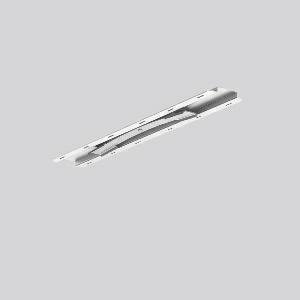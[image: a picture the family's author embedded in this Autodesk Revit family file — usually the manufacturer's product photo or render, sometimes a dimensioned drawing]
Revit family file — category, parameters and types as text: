
# Revit family: linedo_pendelset_verbinder_982680_000_81c2
name_source: partatom
category: Lighting Fixtures
units: mm (PartAtom-declared; Revit-internal decimal feet)

## family parameters
Cut with Voids When Loaded = No
Host = Face
Light Source = No
Part Type = Normal
Room Calculation Point = No
Round Connector Dimension = Use Diameter
Shared = No

## types (1)
- LINEDO Pendelset Verbinder
    Apparent Load = 0 VA
    Default Elevation = 1800 mm
    Description = Connector for suspended installation. Metal lever galvanised to mechanically connect 2 LINEDO suspended modules. A connector must be placed at each joint between modules.
Colour: zinc plated
Length: 300 mm
Width: 48 mm
Height: 9 mm
Weight: 182 g
    Height = 9 mm  [stored 0.0295276 ft]
    Lamp = 0 x
    Length = 300 mm
    Luminous efficacy = 0 lm/W
    Manufacturer = RZB
    ModVariant = No
    Model = 982680.000
    Mounting Place = Ceiling
    Mounting Type = Surface mounted
    Number of Poles = 1
    OnlyDefault = Yes
    Power Factor = 1
    Product Name = LINEDO Pendelset Verbinder
    Product group = Surface mounted continuous line luminaire system
    ProductGroupID = 310
    Protection Class = Protection class
    Protection Degree = Degree of protection
    RLX_Detail_Level = 1
    RLX_Emergency_Light_Flux = 0 lm
    RLX_Emergency_Type = 0
    RLX_Emergency_Type_DB = No
    RlxData = <blob elided: 11345 chars, md5=56dd23d4>
    Standby Power = 0 W
    System Light Flux = 0 lm
    System Power = 0 W
    Type Comments = Product without accessories
    Type Image = 982680.000.jpg
    URL = http://relux.com
    VarID = ---
    Voltage = 0 V
    Weight = 0.00 kg
    Width = 49 mm

note: [stored X ft] marks values corroborated as IEEE doubles in the binary element streams (Revit-internal decimal feet)

## geometry (parser evidence)
native form markers: Sweep x10
no freeform markers — native parametric forms only
